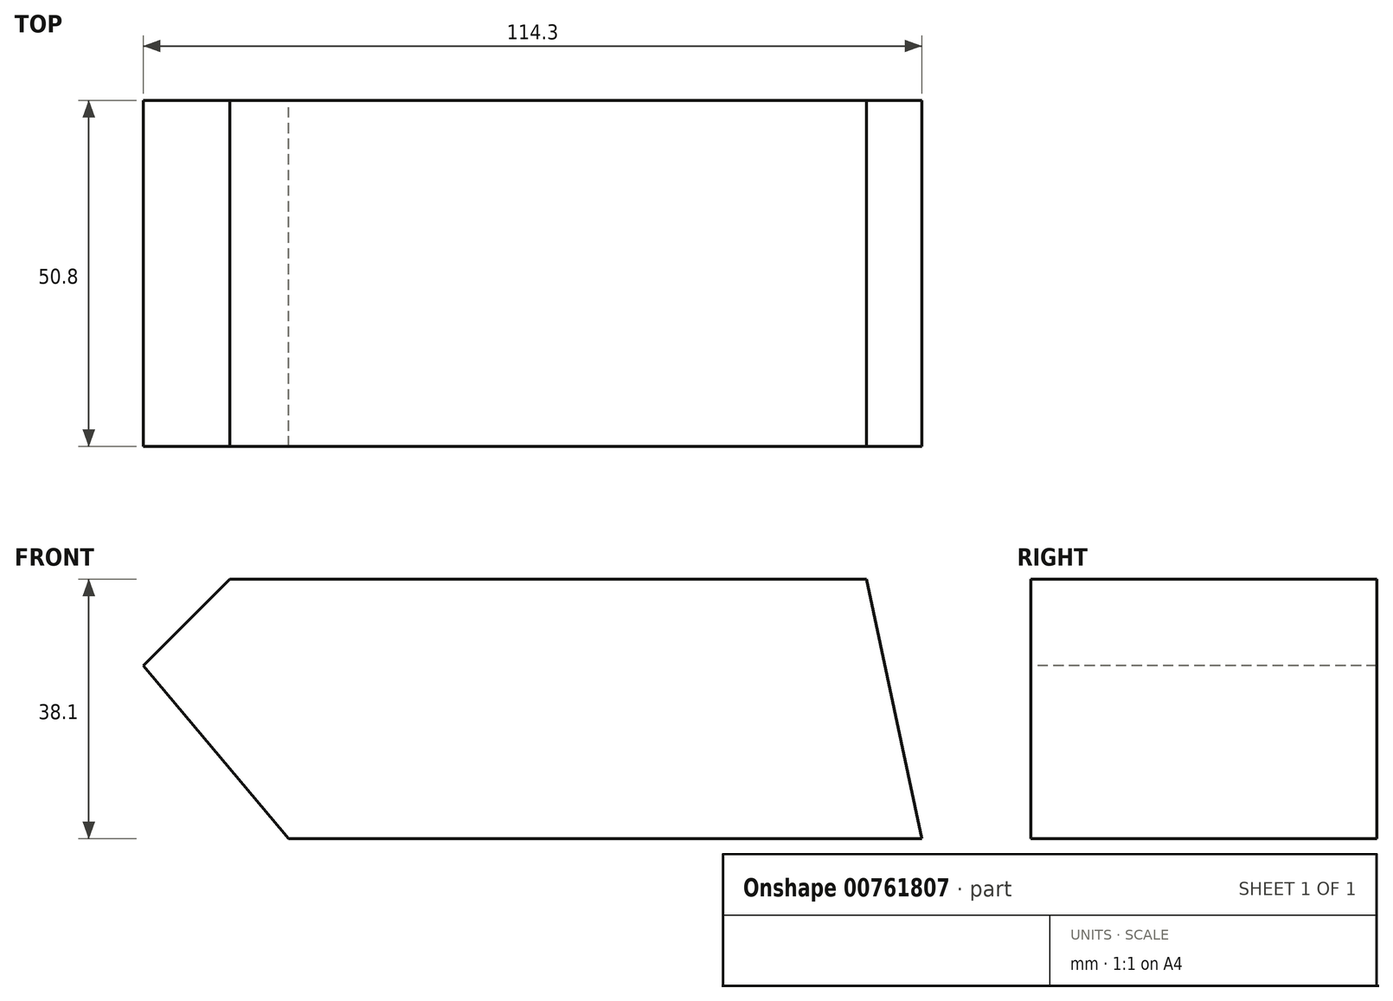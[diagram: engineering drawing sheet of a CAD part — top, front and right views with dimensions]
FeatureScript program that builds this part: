
annotation { "Feature Type Name" : "Feature", "Feature Type Description" : "" }
export const myFeature = defineFeature(function(context is Context, id is Id, definition is map)
    precondition{}
    {
        {
            var Q0;
            Q0=qCreatedBy(makeId("Top.planeOp"),FACE);
            var sketch = newSketch(context, id + "F0", { "sketchPlane" : qUnion([Q0])});
            skLineSegment(sketch, "E0.bottom", {"start": v(-52.43, 24.4) * mm, "end": v(61.87, 24.4) * mm});
            skLineSegment(sketch, "E0.top", {"start": v(-52.43, -26.4) * mm, "end": v(61.87, -26.4) * mm});
            skLineSegment(sketch, "E0.left", {"start": v(-52.43, 24.4) * mm, "end": v(-52.43, -26.4) * mm});
            skLineSegment(sketch, "E0.right", {"start": v(61.87, 24.4) * mm, "end": v(61.87, -26.4) * mm});
            skSolve(sketch);
        }
        {
            var Q0;
            Q0=makeQuery(id+"F0.imprint","IMPRINT",FACE,{"disambiguationData":[TD([[makeQuery(id+"F0.imprint","IMPRINT",EDGE,{"derivedFrom":sQuery(id+"F0.wireOp",EDGE,"E0.bottom")}),-1.0]])]});
            extrude(context, id + "F1", {"entities" : qUnion([Q0]), "depth" : 38.1 * mm, "offsetDistance" : 25.4 * mm});
        }
        {
            var Q0;
            Q0=makeQuery(id+"F1.opExtrude","CAP_EDGE",EDGE,{"disambiguationData":[OSD([sQuery(id+"F0.wireOp",EDGE,"E0.left")])],"isStart":true});
            chamfer(context, id + "F2", {"entities" : qUnion([Q0]), "chamferType" : ChamferType.OFFSET_ANGLE, "width" : 25.4 * mm, "oppositeDirection" : false, "angle" : 40 * degree, "tangentPropagation" : true});
        }
        {
            var Q0;
            Q0=makeQuery(id+"F1.opExtrude","CAP_EDGE",EDGE,{"disambiguationData":[OSD([sQuery(id+"F0.wireOp",EDGE,"E0.left")])],"isStart":false});
            chamfer(context, id + "F3", {"entities" : qUnion([Q0]), "width" : 12.7 * mm, "tangentPropagation" : true});
        }
        {
            var Q0;
            Q0=makeQuery(id+"F1.opExtrude","CAP_EDGE",EDGE,{"disambiguationData":[OSD([sQuery(id+"F0.wireOp",EDGE,"E0.right")])],"isStart":false});
            chamfer(context, id + "F4", {"entities" : qUnion([Q0]), "chamferType" : ChamferType.OFFSET_ANGLE, "width" : 38.1 * mm, "oppositeDirection" : false, "angle" : 12 * degree, "tangentPropagation" : true});
        }
    });
